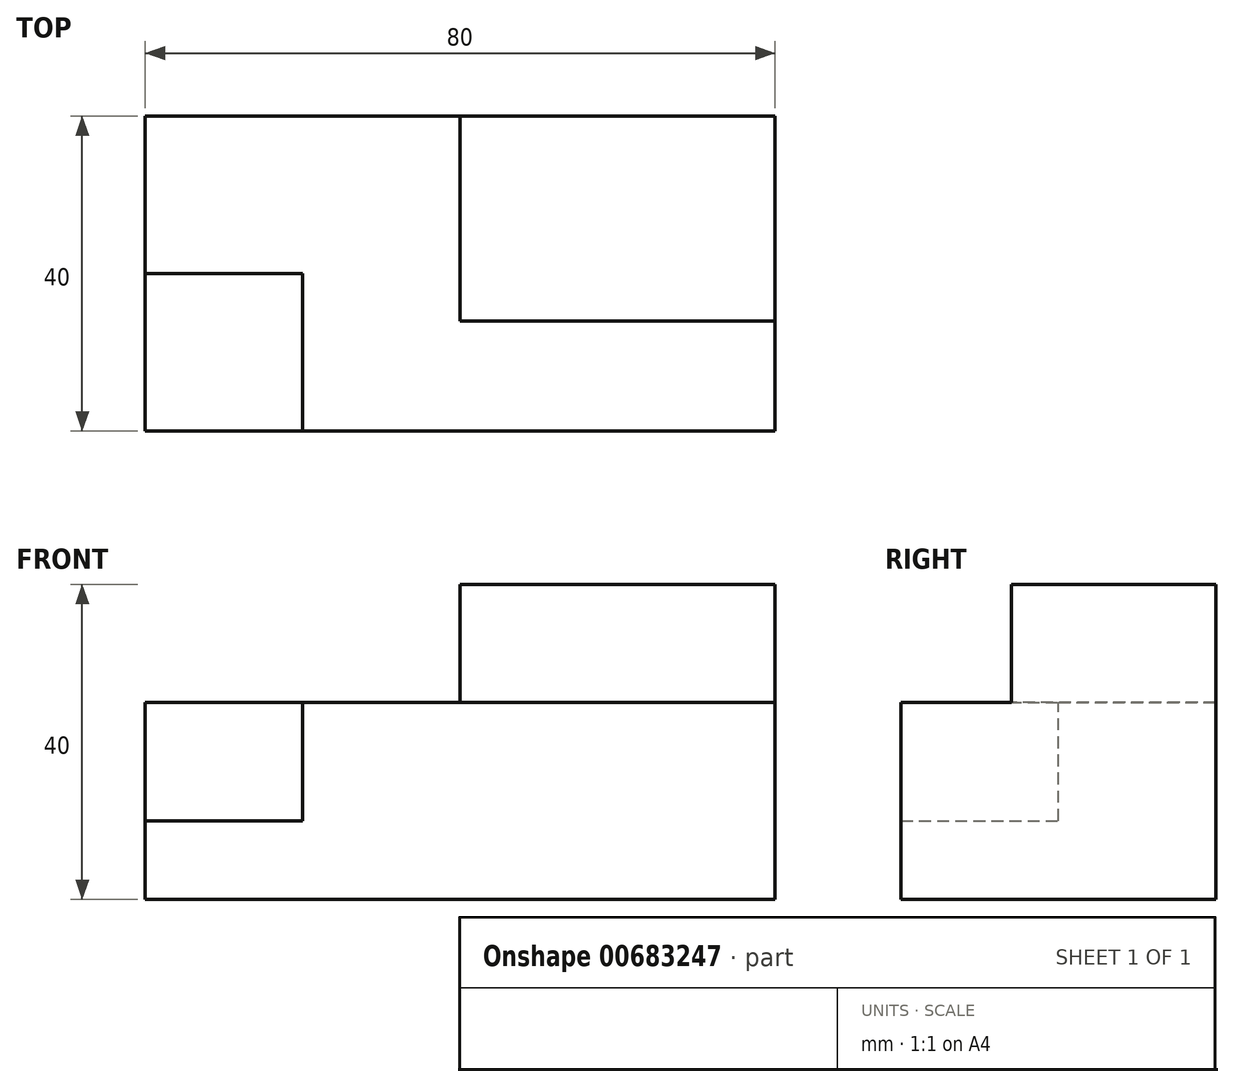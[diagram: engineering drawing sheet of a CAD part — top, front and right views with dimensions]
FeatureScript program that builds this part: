
annotation { "Feature Type Name" : "Feature", "Feature Type Description" : "" }
export const myFeature = defineFeature(function(context is Context, id is Id, definition is map)
    precondition{}
    {
        {
            var Q0;
            Q0=qCreatedBy(makeId("Top.planeOp"),FACE);
            var sketch = newSketch(context, id + "F0", { "sketchPlane" : qUnion([Q0])});
            skLineSegment(sketch, "E0.bottom", {"start": v(0, 0) * mm, "end": v(80, 0) * mm});
            skLineSegment(sketch, "E0.top", {"start": v(0, 40) * mm, "end": v(80, 40) * mm});
            skLineSegment(sketch, "E0.left", {"start": v(0, 0) * mm, "end": v(0, 40) * mm});
            skLineSegment(sketch, "E0.right", {"start": v(80, 0) * mm, "end": v(80, 40) * mm});
            skSolve(sketch);
        }
        {
            var Q0;
            Q0 = qSketchRegion(id + "F0", true);
            extrude(context, id + "F1", {"entities" : qUnion([Q0]), "depth" : 25 * mm, "offsetDistance" : 25 * mm});
        }
        {
            var Q0;
            Q0=makeQuery(id+"F1.opExtrude","CAP_FACE",FACE,{"disambiguationData":[OSD([sQuery(id+"F0.wireOp",EDGE,"E0.bottom"),sQuery(id+"F0.wireOp",EDGE,"E0.top"),sQuery(id+"F0.wireOp",EDGE,"E0.left"),sQuery(id+"F0.wireOp",EDGE,"E0.right")])],"isStart":false});
            var sketch = newSketch(context, id + "F2", { "sketchPlane" : qUnion([Q0])});
            skLineSegment(sketch, "E1.bottom", {"start": v(80, 40) * mm, "end": v(40, 40) * mm});
            skLineSegment(sketch, "E1.top", {"start": v(80, 14) * mm, "end": v(40, 14) * mm});
            skLineSegment(sketch, "E1.left", {"start": v(80, 40) * mm, "end": v(80, 14) * mm});
            skLineSegment(sketch, "E1.right", {"start": v(40, 40) * mm, "end": v(40, 14) * mm});
            skSolve(sketch);
        }
        {
            var Q0;
            Q0 = qSketchRegion(id + "F2", true);
            extrude(context, id + "F3", {"entities" : qUnion([Q0]), "operationType" : NewBodyOperationType.ADD, "depth" : 15 * mm, "offsetDistance" : 25 * mm});
        }
        {
            var Q0;
            Q0=makeQuery(id+"F1.opExtrude","CAP_FACE",FACE,{"disambiguationData":[OSD([sQuery(id+"F0.wireOp",EDGE,"E0.bottom"),sQuery(id+"F0.wireOp",EDGE,"E0.top"),sQuery(id+"F0.wireOp",EDGE,"E0.left"),sQuery(id+"F0.wireOp",EDGE,"E0.right")])],"isStart":false});
            var sketch = newSketch(context, id + "F4", { "sketchPlane" : qUnion([Q0])});
            skLineSegment(sketch, "E2.bottom", {"start": v(0, 0) * mm, "end": v(20, 0) * mm});
            skLineSegment(sketch, "E2.top", {"start": v(0, 20) * mm, "end": v(20, 20) * mm});
            skLineSegment(sketch, "E2.left", {"start": v(0, 0) * mm, "end": v(0, 20) * mm});
            skLineSegment(sketch, "E2.right", {"start": v(20, 0) * mm, "end": v(20, 20) * mm});
            skSolve(sketch);
        }
        {
            var Q0;
            Q0 = qSketchRegion(id + "F4", true);
            extrude(context, id + "F5", {"entities" : qUnion([Q0]), "operationType" : NewBodyOperationType.REMOVE, "oppositeDirection" : true, "depth" : 15 * mm, "offsetDistance" : 25 * mm});
        }
    });
